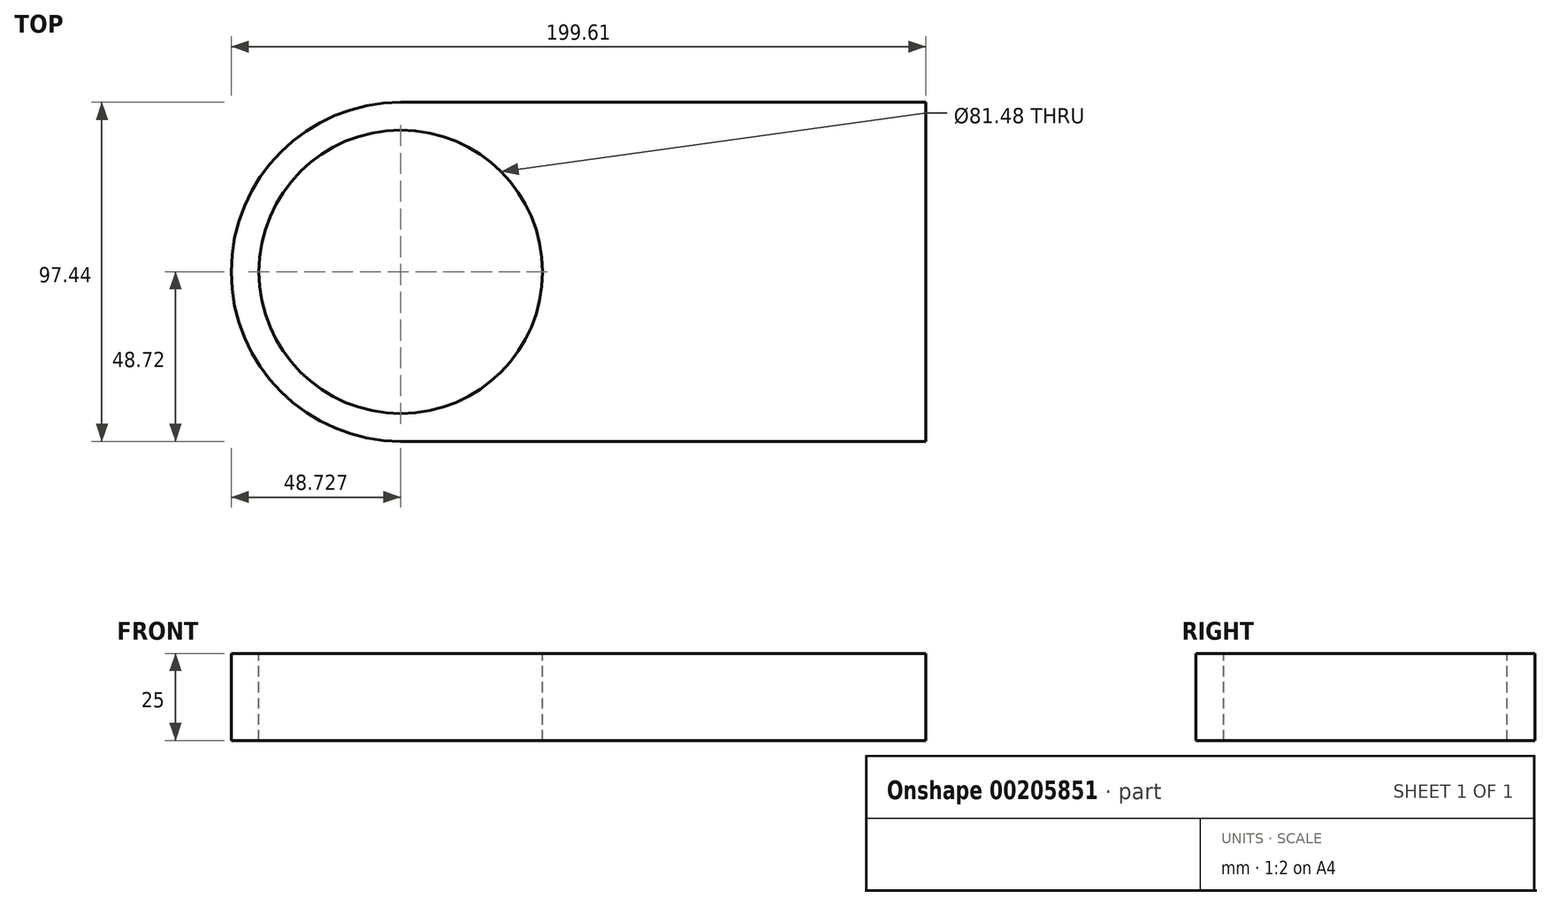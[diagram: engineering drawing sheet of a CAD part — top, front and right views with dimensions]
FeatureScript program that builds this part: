
annotation { "Feature Type Name" : "Feature", "Feature Type Description" : "" }
export const myFeature = defineFeature(function(context is Context, id is Id, definition is map)
    precondition{}
    {
        {
            var Q0;
            Q0=qCreatedBy(makeId("Top.planeOp"),FACE);
            var sketch = newSketch(context, id + "F0", { "sketchPlane" : qUnion([Q0])});
            skLineSegment(sketch, "E0.bottom", {"start": v(-75.44, 48.72) * mm, "end": v(75.44, 48.72) * mm});
            skLineSegment(sketch, "E0.top", {"start": v(-75.44, -48.72) * mm, "end": v(75.44, -48.72) * mm});
            skLineSegment(sketch, "E0.left", {"start": v(-75.44, 48.72) * mm, "end": v(-75.44, -48.72) * mm});
            skLineSegment(sketch, "E0.right", {"start": v(75.44, 48.72) * mm, "end": v(75.44, -48.72) * mm});
            skPoint(sketch, "E0.middle", {"position": v(0, 0) * mm});
            skPoint(sketch, "E1.middle", {"position": v(-75.44, 48.72) * mm});
            skCircle(sketch, "E2", {"center": v(-75.44, 0) * mm, "radius": 48.72 * mm});
            skCircle(sketch, "E3", {"center": v(-75.44, 0) * mm, "radius": 40.74 * mm});
            skSolve(sketch);
        }
        {
            var Q0;
            {var subQ1=sQuery(id+"F0.wireOp",EDGE,"E0.left");var subQ3=sQuery(id+"F0.wireOp",EDGE,"E3");var subQ4=makeQuery(id+"F0.imprint","INTERSECT",VERTEX,{"disambiguationData":[OD(0.0)],"derivedFrom":[subQ1,subQ3]});Q0=makeQuery(id+"F0.imprint","IMPRINT",FACE,{"disambiguationData":[TD([[makeQuery(id+"F0.imprint","IMPRINT",EDGE,{"disambiguationData":[TD([[subQ4,1.0]])],"derivedFrom":subQ3}),-1.0]])]});}
            var Q1;
            {var subQ1=sQuery(id+"F0.wireOp",EDGE,"E0.left");var subQ3=sQuery(id+"F0.wireOp",EDGE,"E3");var subQ4=makeQuery(id+"F0.imprint","INTERSECT",VERTEX,{"disambiguationData":[OD(0.0)],"derivedFrom":[subQ1,subQ3]});Q1=makeQuery(id+"F0.imprint","IMPRINT",FACE,{"disambiguationData":[TD([[makeQuery(id+"F0.imprint","IMPRINT",EDGE,{"disambiguationData":[TD([[subQ4,-1.0]])],"derivedFrom":subQ3}),-1.0]])]});}
            var Q2;
            {var subQ0=sQuery(id+"F0.wireOp",EDGE,"E0.bottom");Q2=makeQuery(id+"F0.imprint","IMPRINT",FACE,{"disambiguationData":[TD([[makeQuery(id+"F0.imprint","IMPRINT",EDGE,{"derivedFrom":subQ0}),-1.0]])]});}
            extrude(context, id + "F1", {"entities" : qUnion([Q0, Q1, Q2]), "oppositeDirection" : true, "depth" : 25 * mm, "offsetDistance" : 25 * mm});
        }
    });
